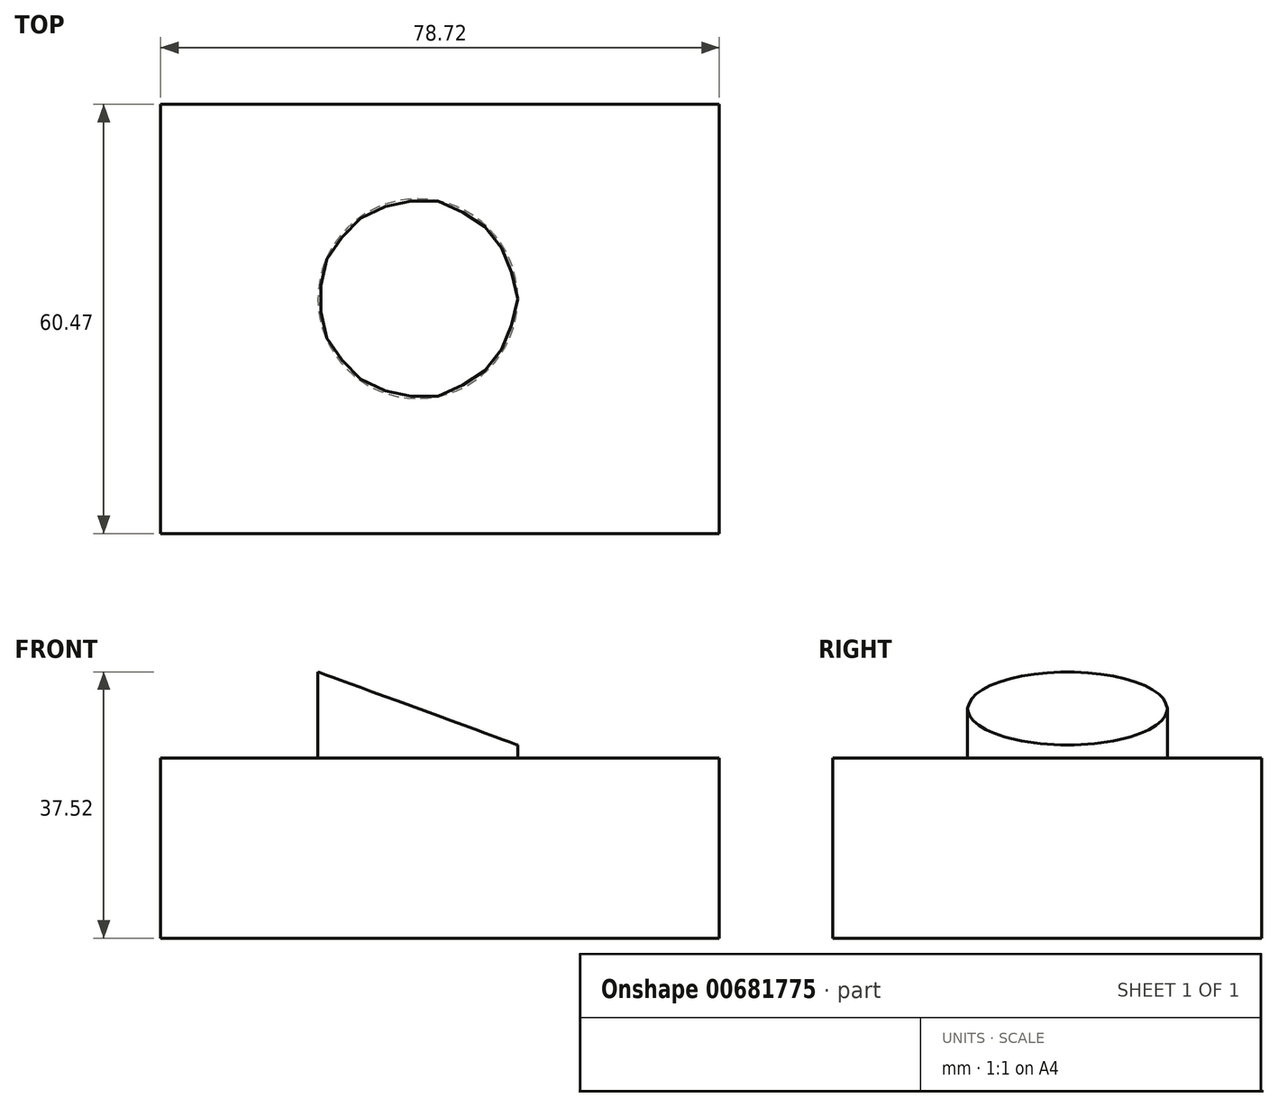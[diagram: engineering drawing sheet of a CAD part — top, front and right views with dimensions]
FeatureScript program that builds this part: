
annotation { "Feature Type Name" : "Feature", "Feature Type Description" : "" }
export const myFeature = defineFeature(function(context is Context, id is Id, definition is map)
    precondition{}
    {
        {
            var Q0;
            Q0=qCreatedBy(makeId("Top.planeOp"),FACE);
            var sketch = newSketch(context, id + "F0", { "sketchPlane" : qUnion([Q0])});
            skLineSegment(sketch, "E0.bottom", {"start": v(-43.6, 27.38) * mm, "end": v(35.12, 27.38) * mm});
            skLineSegment(sketch, "E0.top", {"start": v(-43.6, -33.1) * mm, "end": v(35.12, -33.1) * mm});
            skLineSegment(sketch, "E0.left", {"start": v(-43.6, 27.38) * mm, "end": v(-43.6, -33.1) * mm});
            skLineSegment(sketch, "E0.right", {"start": v(35.12, 27.38) * mm, "end": v(35.12, -33.1) * mm});
            skSolve(sketch);
        }
        {
            var Q0;
            Q0=makeQuery(id+"F0.imprint","IMPRINT",FACE,{"disambiguationData":[TD([[makeQuery(id+"F0.imprint","IMPRINT",EDGE,{"derivedFrom":sQuery(id+"F0.wireOp",EDGE,"E0.bottom")}),-1.0]])]});
            extrude(context, id + "F1", {"entities" : qUnion([Q0]), "depth" : 25.4 * mm, "offsetDistance" : 25.4 * mm});
        }
        {
            var Q0;
            Q0=makeQuery(id+"F1.opExtrude","CAP_FACE",FACE,{"disambiguationData":[OSD([sQuery(id+"F0.wireOp",EDGE,"E0.bottom"),sQuery(id+"F0.wireOp",EDGE,"E0.top"),sQuery(id+"F0.wireOp",EDGE,"E0.left"),sQuery(id+"F0.wireOp",EDGE,"E0.right")])],"isStart":false});
            var sketch = newSketch(context, id + "F2", { "sketchPlane" : qUnion([Q0])});
            skCircle(sketch, "E1", {"center": v(-7.36, 0) * mm, "radius": 14.07 * mm});
            skSolve(sketch);
        }
        {
            var Q0;
            Q0 = qSketchRegion(id + "F2", true);
            extrude(context, id + "F3", {"entities" : qUnion([Q0]), "operationType" : NewBodyOperationType.ADD, "depth" : 12.7 * mm, "offsetDistance" : 25.4 * mm});
        }
        {
            var Q0;
            Q0=qCreatedBy(makeId("Front.planeOp"),FACE);
            var sketch = newSketch(context, id + "F4", { "sketchPlane" : qUnion([Q0])});
            skLineSegment(sketch, "E2", {"start": v(-30.67, 40.9) * mm, "end": v(8.41, 26.6) * mm});
            skLineSegment(sketch, "E3", {"start": v(8.41, 26.6) * mm, "end": v(8.41, 43.52) * mm});
            skLineSegment(sketch, "E4", {"start": v(8.41, 43.52) * mm, "end": v(-25.9, 39.15) * mm});
            skSolve(sketch);
        }
        {
            var Q0;
            Q0 = qSketchRegion(id + "F4", true);
            extrude(context, id + "F5", {"entities" : qUnion([Q0]), "operationType" : NewBodyOperationType.REMOVE, "depth" : 25.4 * mm, "offsetDistance" : 25.4 * mm});
        }
        {
            var Q0;
            Q0=makeQuery(id+"F5.boolean.opBoolean","COPY",FACE,{"derivedFrom":makeQuery(id+"F5.opExtrude","CAP_FACE",FACE,{"disambiguationData":[OSD([sQuery(id+"F4.wireOp",EDGE,"E2"),sQuery(id+"F4.wireOp",EDGE,"E3"),sQuery(id+"F4.wireOp",EDGE,"E4")])],"isStart":true})});
            var sketch = newSketch(context, id + "F6", { "sketchPlane" : qUnion([Q0])});
            skSolve(sketch);
        }
        {
            var Q0;
            {var subQ0=sQuery(id+"F4.wireOp",EDGE,"E2");Q0=makeQuery(id+"F6.imprint","IMPRINT",FACE,{"disambiguationData":[TD([[makeQuery(id+"F6.imprint","IMPRINT",EDGE,{"derivedFrom":makeQuery(id+"F5.boolean.opBoolean","COPY",EDGE,{"derivedFrom":makeQuery(id+"F5.opExtrude","CAP_EDGE",EDGE,{"disambiguationData":[OSD([subQ0])],"isStart":true})})}),1.0]])]});}
            extrude(context, id + "F7", {"entities" : qUnion([Q0]), "operationType" : NewBodyOperationType.REMOVE, "oppositeDirection" : true, "depth" : 25.4 * mm, "offsetDistance" : 25.4 * mm});
        }
    });
